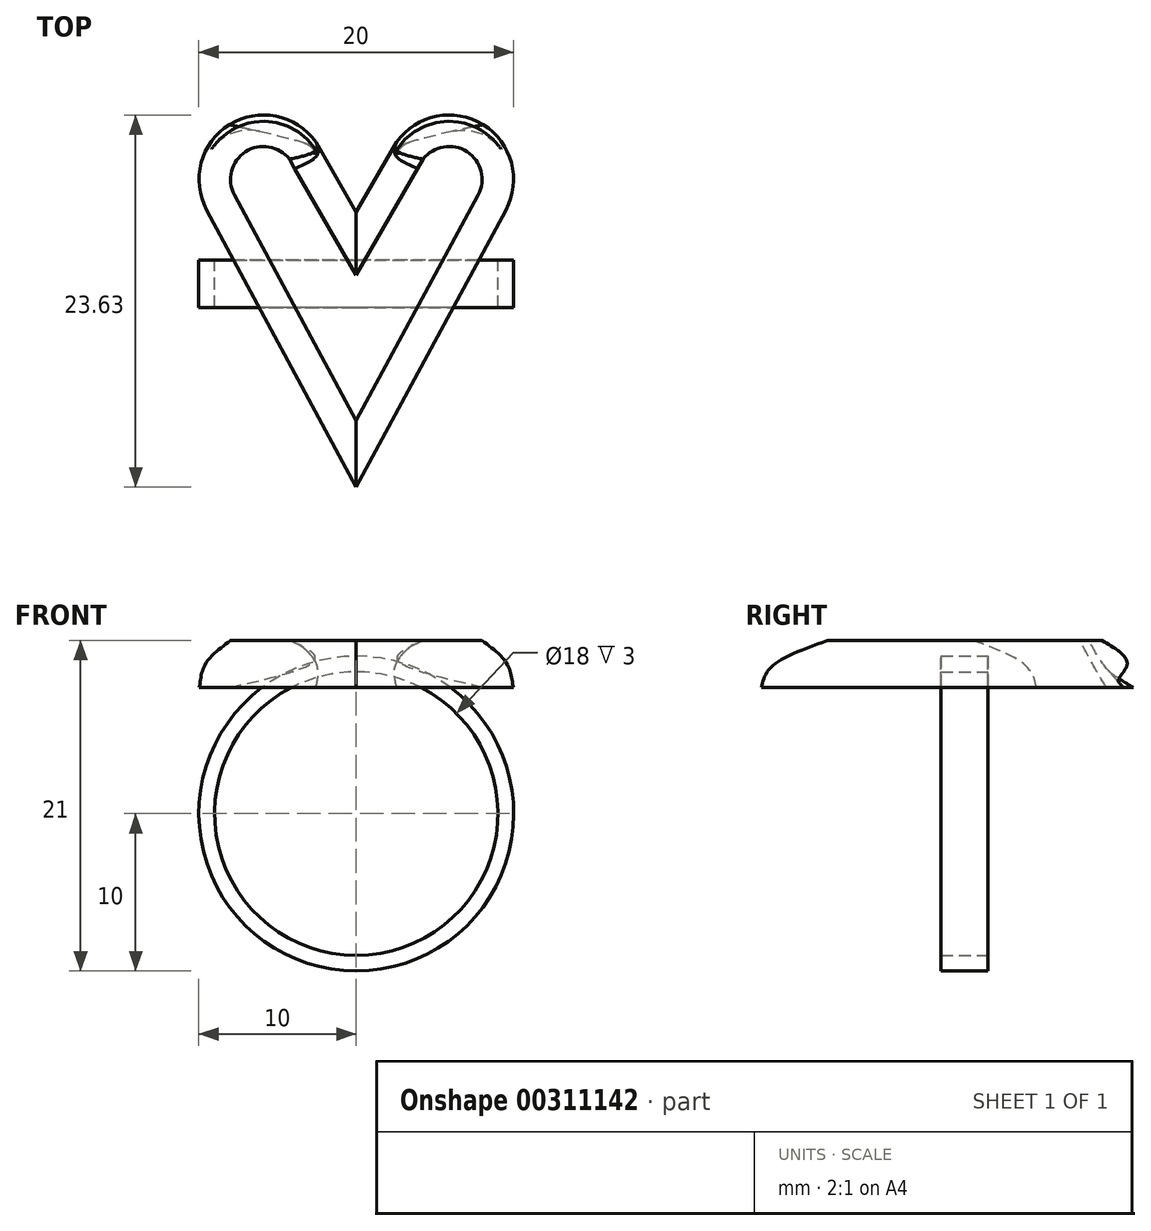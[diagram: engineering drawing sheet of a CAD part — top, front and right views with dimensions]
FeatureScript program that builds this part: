
annotation { "Feature Type Name" : "Feature", "Feature Type Description" : "" }
export const myFeature = defineFeature(function(context is Context, id is Id, definition is map)
    precondition{}
    {
        {
            var Q0;
            Q0=qCreatedBy(makeId("Top.planeOp"),FACE);
            var sketch = newSketch(context, id + "F0", { "sketchPlane" : qUnion([Q0])});
            skLineSegment(sketch, "E0", {"start": v(0, 0) * mm, "end": v(0, 13.4) * mm, "construction": true});
            skPoint(sketch, "E1", {"position": v(0, -6.6) * mm});
            skLineSegment(sketch, "E2", {"start": v(-9.5, 11) * mm, "end": v(0, -6.6) * mm});
            skLineSegment(sketch, "E3", {"start": v(9.5, 11) * mm, "end": v(0, -6.6) * mm});
            skLineSegment(sketch, "E4", {"start": v(0, 10.87) * mm, "end": v(-4.34, 18.4) * mm});
            skArc(sketch, "E5", {"start": v(-2.17, 14.63) * mm, "mid": v(-7.71, 16.6) * mm, "end": v(-9.5, 11) * mm});
            skLineSegment(sketch, "E6.MirrorCS", {"start": v(0, 10.87) * mm, "end": v(4.34, 18.4) * mm});
            skArc(sketch, "E7.MirrorCS", {"start": v(2.17, 14.63) * mm, "mid": v(7.71, 16.6) * mm, "end": v(9.5, 11) * mm});
            skSolve(sketch);
        }
        {
            var Q0;
            Q0=qCreatedBy(makeId("Top.planeOp"),FACE);
            cPlane(context, id + "F1", {"entities" : qUnion([Q0]), "cplaneType" : CPlaneType.OFFSET, "offset" : 1.5 * mm, "width" : 150 * mm, "height" : 150 * mm});
        }
        {
            var Q0;
            Q0=qCreatedBy(makeId("Top.planeOp"),FACE);
            cPlane(context, id + "F2", {"entities" : qUnion([Q0]), "cplaneType" : CPlaneType.OFFSET, "offset" : 3 * mm, "width" : 150 * mm, "height" : 150 * mm});
        }
        {
            var Q0;
            Q0=qCreatedBy(id+"F2.planeOp",FACE);
            var sketch = newSketch(context, id + "F3", { "sketchPlane" : qUnion([Q0])});
            skLineSegment(sketch, "E8.0", {"start": v(4.24, 14.22) * mm, "end": v(3.9, 13.63) * mm});
            skArc(sketch, "E8.1", {"start": v(7.73, 11.95) * mm, "mid": v(7.03, 14.7) * mm, "end": v(4.24, 14.22) * mm});
            skLineSegment(sketch, "E8.2", {"start": v(3.9, 13.63) * mm, "end": v(0, 6.87) * mm});
            skLineSegment(sketch, "E8.3", {"start": v(0, -2.4) * mm, "end": v(7.73, 11.95) * mm});
            skLineSegment(sketch, "E8.4", {"start": v(0, 6.87) * mm, "end": v(-3.9, 13.63) * mm});
            skLineSegment(sketch, "E8.5", {"start": v(-3.9, 13.63) * mm, "end": v(-4.24, 14.22) * mm});
            skArc(sketch, "E8.6", {"start": v(-4.24, 14.22) * mm, "mid": v(-7.03, 14.7) * mm, "end": v(-7.73, 11.95) * mm});
            skLineSegment(sketch, "E8.7", {"start": v(-7.73, 11.95) * mm, "end": v(0, -2.4) * mm});
            skSolve(sketch);
        }
        {
            var Q0;
            Q0=qCreatedBy(id+"F1.planeOp",FACE);
            var sketch = newSketch(context, id + "F4", { "sketchPlane" : qUnion([Q0])});
            skPoint(sketch, "E9", {"position": v(0, 24.6) * mm});
            skLineSegment(sketch, "E10.0", {"start": v(2.9, 15.1) * mm, "end": v(2.52, 14.43) * mm});
            skArc(sketch, "E10.1", {"start": v(9.14, 11.19) * mm, "mid": v(7.86, 16.07) * mm, "end": v(2.9, 15.1) * mm});
            skLineSegment(sketch, "E10.2", {"start": v(2.52, 14.43) * mm, "end": v(0, 10.07) * mm});
            skLineSegment(sketch, "E10.3", {"start": v(0, -5.76) * mm, "end": v(9.14, 11.19) * mm});
            skLineSegment(sketch, "E10.4", {"start": v(0, 10.07) * mm, "end": v(-2.52, 14.43) * mm});
            skLineSegment(sketch, "E10.5", {"start": v(-2.52, 14.43) * mm, "end": v(-2.9, 15.1) * mm});
            skArc(sketch, "E10.6", {"start": v(-2.9, 15.1) * mm, "mid": v(-7.86, 16.07) * mm, "end": v(-9.14, 11.19) * mm});
            skLineSegment(sketch, "E10.7", {"start": v(-9.14, 11.19) * mm, "end": v(0, -5.76) * mm});
            skSolve(sketch);
        }
        {
            var Q0;
            Q0=qCreatedBy(makeId("Front.planeOp"),FACE);
            cPlane(context, id + "F5", {"entities" : qUnion([Q0]), "cplaneType" : CPlaneType.OFFSET, "offset" : 7.8 * mm, "oppositeDirection" : true, "width" : 152.4 * mm, "height" : 152.4 * mm});
        }
        {
            var Q0;
            Q0=qCreatedBy(id+"F5.planeOp",FACE);
            var sketch = newSketch(context, id + "F6", { "sketchPlane" : qUnion([Q0])});
            skCircle(sketch, "E11", {"center": v(0, -8) * mm, "radius": 9 * mm});
            skPoint(sketch, "E12", {"position": v(0, -17) * mm});
            skPoint(sketch, "E13", {"position": v(0, 1) * mm});
            skCircle(sketch, "E14", {"center": v(0, -8) * mm, "radius": 10 * mm});
            skSolve(sketch);
        }
        {
            var Q0;
            {var subQ7=sQuery(id+"F0.wireOp",EDGE,"E2");Q0=makeQuery(id+"F0.imprint","IMPRINT",FACE,{"disambiguationData":[TD([[makeQuery(id+"F0.imprint","IMPRINT",EDGE,{"derivedFrom":subQ7}),1.0]])]});}
            var Q1;
            Q1=makeQuery(id+"F4.imprint","IMPRINT",FACE,{"disambiguationData":[TD([[makeQuery(id+"F4.imprint","IMPRINT",EDGE,{"derivedFrom":sQuery(id+"F4.wireOp",EDGE,"E10.0")}),1.0]])]});
            var Q2;
            Q2=makeQuery(id+"F3.imprint","IMPRINT",FACE,{"disambiguationData":[TD([[makeQuery(id+"F3.imprint","IMPRINT",EDGE,{"derivedFrom":sQuery(id+"F3.wireOp",EDGE,"E8.0")}),1.0]])]});
            loft(context, id + "F7", {"sheetProfilesArray" : [{ "sheetProfileEntities" : qUnion([Q0]) }, { "sheetProfileEntities" : qUnion([Q1]) }, { "sheetProfileEntities" : qUnion([Q2]) }]});
        }
        {
            var Q0;
            Q0=makeQuery(id+"F6.imprint","IMPRINT",FACE,{"disambiguationData":[TD([[makeQuery(id+"F6.imprint","IMPRINT",EDGE,{"derivedFrom":sQuery(id+"F6.wireOp",EDGE,"E11")}),-1.0]])]});
            extrude(context, id + "F8", {"entities" : qUnion([Q0]), "depth" : 3 * mm});
        }
    });
